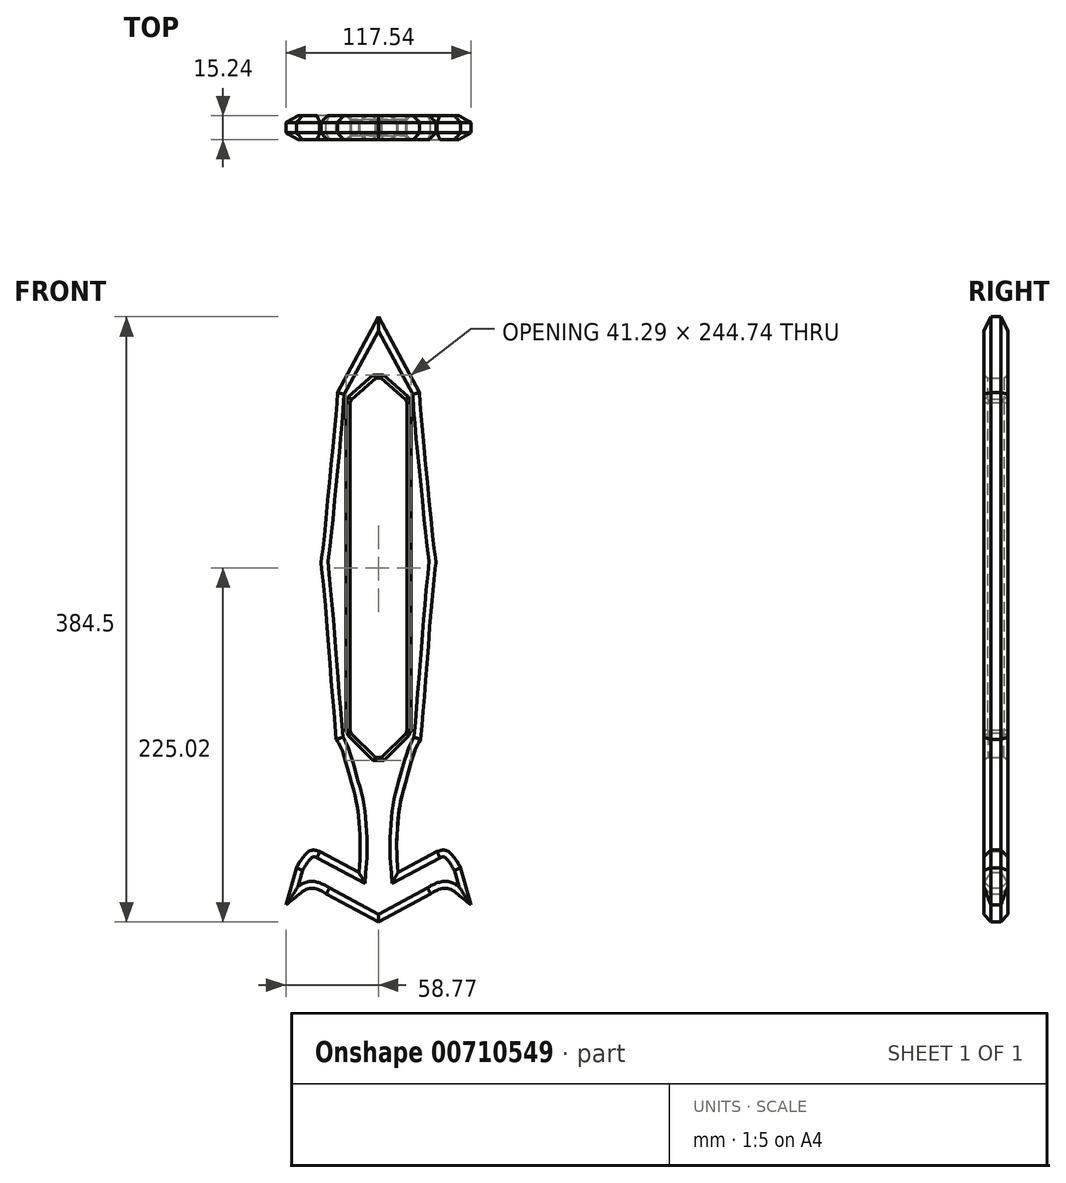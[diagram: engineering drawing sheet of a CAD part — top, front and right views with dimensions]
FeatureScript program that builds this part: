
annotation { "Feature Type Name" : "Feature", "Feature Type Description" : "" }
export const myFeature = defineFeature(function(context is Context, id is Id, definition is map)
    precondition{}
    {
        {
            var Q0;
            Q0=qCreatedBy(makeId("Front.planeOp"),FACE);
            var sketch = newSketch(context, id + "F0", { "sketchPlane" : qUnion([Q0])});
            skFitSpline(sketch, "E0", {"points": [v(-58.77, 10.9) * mm, v(-52.04, 16.33) * mm, v(-46.35, 20.47) * mm, v(-42.08, 21.5) * mm, v(-37.3, 20.2) * mm, v(-33.15, 18) * mm], "startDerivative": vector(27.97, 22.48) * mm, "endDerivative": vector(22.23, -12.93) * mm});
            skLineSegment(sketch, "E1", {"start": v(-33.15, 18) * mm, "end": v(0, 0) * mm});
            skLineSegment(sketch, "E2", {"start": v(0, 0) * mm, "end": v(0, 6.5) * mm});
            skLineSegment(sketch, "E3", {"start": v(-58.77, 10.9) * mm, "end": v(-52.17, 34.44) * mm});
            skFitSpline(sketch, "E4", {"points": [v(-52.17, 34.44) * mm, v(-48.35, 40.7) * mm, v(-44.15, 44.9) * mm, v(-40.76, 45.72) * mm, v(-37.26, 44.79) * mm], "startDerivative": vector(11.84, 21.29) * mm, "endDerivative": vector(16.46, -5.96) * mm});
            skLineSegment(sketch, "E5", {"start": v(-37.26, 44.79) * mm, "end": v(-12.38, 31.59) * mm});
            skFitSpline(sketch, "E6", {"points": [v(-12.38, 31.59) * mm, v(-11.57, 45.95) * mm, v(-12.01, 59.35) * mm, v(-13.24, 72.07) * mm, v(-15.2, 81.42) * mm, v(-20.04, 98.98) * mm, v(-23.62, 110.2) * mm, v(-26.8, 116.07) * mm], "startDerivative": vector(7.18, 93.5) * mm, "endDerivative": vector(-31.36, 51.49) * mm});
            skFitSpline(sketch, "E7", {"points": [v(-26.8, 116.07) * mm, v(-28.43, 135.58) * mm, v(-30.56, 161.2) * mm, v(-33.27, 195.81) * mm, v(-36.38, 226.72) * mm, v(-36.58, 228.72) * mm, v(-36.26, 231.14) * mm, v(-34.94, 240.06) * mm, v(-32.21, 267.55) * mm, v(-29.1, 299.32) * mm, v(-26.8, 324.09) * mm, v(-26.1, 336.42) * mm], "startDerivative": vector(-16.49, 198.18) * mm, "endDerivative": vector(6.55, 149.17) * mm});
            skLineSegment(sketch, "E8", {"start": v(-26.1, 336.42) * mm, "end": v(0, 384.5) * mm});
            skLineSegment(sketch, "E9.MirrorCS", {"start": v(33.15, 18) * mm, "end": v(0, 0) * mm});
            skFitSpline(sketch, "E10.MirrorCS", {"points": [v(58.77, 10.9) * mm, v(52.04, 16.33) * mm, v(46.35, 20.47) * mm, v(42.08, 21.5) * mm, v(37.3, 20.2) * mm, v(33.15, 18) * mm], "startDerivative": vector(-27.97, 22.48) * mm, "endDerivative": vector(-22.23, -12.93) * mm});
            skLineSegment(sketch, "E11.MirrorCS", {"start": v(37.26, 44.79) * mm, "end": v(12.38, 31.59) * mm});
            skLineSegment(sketch, "E12.MirrorCS", {"start": v(58.77, 10.9) * mm, "end": v(52.17, 34.44) * mm});
            skFitSpline(sketch, "E13.MirrorCS", {"points": [v(52.17, 34.44) * mm, v(48.35, 40.7) * mm, v(44.15, 44.9) * mm, v(40.76, 45.72) * mm, v(37.26, 44.79) * mm], "startDerivative": vector(-11.84, 21.29) * mm, "endDerivative": vector(-16.46, -5.96) * mm});
            skFitSpline(sketch, "E14.MirrorCS", {"points": [v(12.38, 31.59) * mm, v(11.57, 45.95) * mm, v(12.01, 59.35) * mm, v(13.24, 72.07) * mm, v(15.2, 81.42) * mm, v(20.04, 98.98) * mm, v(23.62, 110.2) * mm, v(26.8, 116.07) * mm], "startDerivative": vector(-7.18, 93.5) * mm, "endDerivative": vector(31.36, 51.49) * mm});
            skFitSpline(sketch, "E15.MirrorCS", {"points": [v(26.8, 116.07) * mm, v(28.43, 135.58) * mm, v(30.56, 161.2) * mm, v(33.27, 195.81) * mm, v(36.38, 226.72) * mm, v(36.58, 228.72) * mm, v(36.26, 231.14) * mm, v(34.94, 240.06) * mm, v(32.21, 267.55) * mm, v(29.1, 299.32) * mm, v(26.8, 324.09) * mm, v(26.1, 336.42) * mm], "startDerivative": vector(16.49, 198.18) * mm, "endDerivative": vector(-6.55, 149.17) * mm});
            skLineSegment(sketch, "E16.MirrorCS", {"start": v(26.1, 336.42) * mm, "end": v(0, 384.5) * mm});
            skSolve(sketch);
        }
        {
            var Q0;
            Q0=makeQuery(id+"F0.imprint","IMPRINT",FACE,{"disambiguationData":[TD([[makeQuery(id+"F0.imprint","IMPRINT",EDGE,{"derivedFrom":sQuery(id+"F0.wireOp",EDGE,"E0")}),1.0]])]});
            extrude(context, id + "F1", {"entities" : qUnion([Q0]), "endBound" : BoundingType.SYMMETRIC, "depth" : 15.24 * mm, "offsetDistance" : 25.4 * mm});
        }
        {
            var Q0;
            Q0=makeQuery(id+"F1.opExtrude","CAP_FACE",FACE,{"disambiguationData":[OSD([sQuery(id+"F0.wireOp",EDGE,"E0"),sQuery(id+"F0.wireOp",EDGE,"E1"),sQuery(id+"F0.wireOp",EDGE,"E3"),sQuery(id+"F0.wireOp",EDGE,"E4"),sQuery(id+"F0.wireOp",EDGE,"E5"),sQuery(id+"F0.wireOp",EDGE,"E6"),sQuery(id+"F0.wireOp",EDGE,"E7"),sQuery(id+"F0.wireOp",EDGE,"E8"),sQuery(id+"F0.wireOp",EDGE,"E9.MirrorCS"),sQuery(id+"F0.wireOp",EDGE,"E10.MirrorCS"),sQuery(id+"F0.wireOp",EDGE,"E11.MirrorCS"),sQuery(id+"F0.wireOp",EDGE,"E12.MirrorCS"),sQuery(id+"F0.wireOp",EDGE,"E13.MirrorCS"),sQuery(id+"F0.wireOp",EDGE,"E14.MirrorCS"),sQuery(id+"F0.wireOp",EDGE,"E15.MirrorCS"),sQuery(id+"F0.wireOp",EDGE,"E16.MirrorCS")])],"isStart":true});
            var Q1;
            Q1=makeQuery(id+"F1.opExtrude","CAP_FACE",FACE,{"disambiguationData":[OSD([sQuery(id+"F0.wireOp",EDGE,"E0"),sQuery(id+"F0.wireOp",EDGE,"E1"),sQuery(id+"F0.wireOp",EDGE,"E3"),sQuery(id+"F0.wireOp",EDGE,"E4"),sQuery(id+"F0.wireOp",EDGE,"E5"),sQuery(id+"F0.wireOp",EDGE,"E6"),sQuery(id+"F0.wireOp",EDGE,"E7"),sQuery(id+"F0.wireOp",EDGE,"E8"),sQuery(id+"F0.wireOp",EDGE,"E9.MirrorCS"),sQuery(id+"F0.wireOp",EDGE,"E10.MirrorCS"),sQuery(id+"F0.wireOp",EDGE,"E11.MirrorCS"),sQuery(id+"F0.wireOp",EDGE,"E12.MirrorCS"),sQuery(id+"F0.wireOp",EDGE,"E13.MirrorCS"),sQuery(id+"F0.wireOp",EDGE,"E14.MirrorCS"),sQuery(id+"F0.wireOp",EDGE,"E15.MirrorCS"),sQuery(id+"F0.wireOp",EDGE,"E16.MirrorCS")])],"isStart":false});
            chamfer(context, id + "F2", {"entities" : qUnion([Q0, Q1]), "chamferType" : ChamferType.OFFSET_ANGLE, "width" : 4.32 * mm, "oppositeDirection" : false, "angle" : 45 * degree, "tangentPropagation" : true});
        }
        {
            var Q0;
            Q0=qCreatedBy(makeId("Front.planeOp"),FACE);
            var sketch = newSketch(context, id + "F3", { "sketchPlane" : qUnion([Q0])});
            skLineSegment(sketch, "E17", {"start": v(0, 102.67) * mm, "end": v(18.1, 120.66) * mm});
            skLineSegment(sketch, "E18", {"start": v(18.1, 120.66) * mm, "end": v(18.1, 331.1) * mm});
            skLineSegment(sketch, "E19", {"start": v(18.1, 331.1) * mm, "end": v(0, 346.95) * mm});
            skLineSegment(sketch, "E20", {"start": v(0, 346.95) * mm, "end": v(0, 335.17) * mm});
            skLineSegment(sketch, "E21.MirrorCS", {"start": v(-18.1, 331.1) * mm, "end": v(0, 346.95) * mm});
            skLineSegment(sketch, "E22.MirrorCS", {"start": v(-18.1, 120.66) * mm, "end": v(-18.1, 331.1) * mm});
            skLineSegment(sketch, "E23.MirrorCS", {"start": v(0, 102.67) * mm, "end": v(-18.1, 120.66) * mm});
            skSolve(sketch);
        }
        {
            var Q0;
            Q0=makeQuery(id+"F3.imprint","IMPRINT",FACE,{"disambiguationData":[TD([[makeQuery(id+"F3.imprint","IMPRINT",EDGE,{"derivedFrom":sQuery(id+"F3.wireOp",EDGE,"E17")}),1.0]])]});
            extrude(context, id + "F4", {"entities" : qUnion([Q0]), "operationType" : NewBodyOperationType.REMOVE, "oppositeDirection" : true, "depth" : 25.4 * mm, "offsetDistance" : 25.4 * mm});
        }
        {
            var Q0;
            Q0=makeQuery(id+"F4.boolean.opBoolean","COPY",FACE,{"derivedFrom":makeQuery(id+"F4.opExtrude","CAP_FACE",FACE,{"disambiguationData":[OSD([sQuery(id+"F3.wireOp",EDGE,"E17"),sQuery(id+"F3.wireOp",EDGE,"E18"),sQuery(id+"F3.wireOp",EDGE,"E19"),sQuery(id+"F3.wireOp",EDGE,"E21.MirrorCS"),sQuery(id+"F3.wireOp",EDGE,"E22.MirrorCS"),sQuery(id+"F3.wireOp",EDGE,"E23.MirrorCS")])],"isStart":true})});
            extrude(context, id + "F5", {"entities" : qUnion([Q0]), "operationType" : NewBodyOperationType.REMOVE, "oppositeDirection" : true, "depth" : 25.4 * mm, "offsetDistance" : 25.4 * mm});
        }
        {
            var Q0;
            {var subQ0=sQuery(id+"F3.wireOp",EDGE,"E22.MirrorCS");Q0=makeQuery(id+"F5.boolean.opBoolean","MERGE",FACE,{"derivedFrom":[makeQuery(id+"F4.boolean.opBoolean","COPY",FACE,{"derivedFrom":makeQuery(id+"F4.opExtrude","SWEPT_FACE",FACE,{"disambiguationData":[OSD([subQ0])]})})],"fromTools":[makeQuery(id+"F5.opExtrude","SWEPT_FACE",FACE,{"disambiguationData":[OSD([subQ0])]})]});}
            var Q1;
            {var subQ0=sQuery(id+"F3.wireOp",EDGE,"E23.MirrorCS");Q1=makeQuery(id+"F5.boolean.opBoolean","MERGE",FACE,{"derivedFrom":[makeQuery(id+"F4.boolean.opBoolean","COPY",FACE,{"derivedFrom":makeQuery(id+"F4.opExtrude","SWEPT_FACE",FACE,{"disambiguationData":[OSD([subQ0])]})})],"fromTools":[makeQuery(id+"F5.opExtrude","SWEPT_FACE",FACE,{"disambiguationData":[OSD([subQ0])]})]});}
            var Q2;
            {var subQ0=sQuery(id+"F3.wireOp",EDGE,"E21.MirrorCS");Q2=makeQuery(id+"F5.boolean.opBoolean","MERGE",FACE,{"derivedFrom":[makeQuery(id+"F4.boolean.opBoolean","COPY",FACE,{"derivedFrom":makeQuery(id+"F4.opExtrude","SWEPT_FACE",FACE,{"disambiguationData":[OSD([subQ0])]})})],"fromTools":[makeQuery(id+"F5.opExtrude","SWEPT_FACE",FACE,{"disambiguationData":[OSD([subQ0])]})]});}
            var Q3;
            {var subQ0=sQuery(id+"F3.wireOp",EDGE,"E19");Q3=makeQuery(id+"F5.boolean.opBoolean","MERGE",FACE,{"derivedFrom":[makeQuery(id+"F4.boolean.opBoolean","COPY",FACE,{"derivedFrom":makeQuery(id+"F4.opExtrude","SWEPT_FACE",FACE,{"disambiguationData":[OSD([subQ0])]})})],"fromTools":[makeQuery(id+"F5.opExtrude","SWEPT_FACE",FACE,{"disambiguationData":[OSD([subQ0])]})]});}
            var Q4;
            {var subQ0=sQuery(id+"F3.wireOp",EDGE,"E18");Q4=makeQuery(id+"F5.boolean.opBoolean","MERGE",FACE,{"derivedFrom":[makeQuery(id+"F4.boolean.opBoolean","COPY",FACE,{"derivedFrom":makeQuery(id+"F4.opExtrude","SWEPT_FACE",FACE,{"disambiguationData":[OSD([subQ0])]})})],"fromTools":[makeQuery(id+"F5.opExtrude","SWEPT_FACE",FACE,{"disambiguationData":[OSD([subQ0])]})]});}
            var Q5;
            {var subQ0=sQuery(id+"F3.wireOp",EDGE,"E17");Q5=makeQuery(id+"F5.boolean.opBoolean","MERGE",FACE,{"derivedFrom":[makeQuery(id+"F4.boolean.opBoolean","COPY",FACE,{"derivedFrom":makeQuery(id+"F4.opExtrude","SWEPT_FACE",FACE,{"disambiguationData":[OSD([subQ0])]})})],"fromTools":[makeQuery(id+"F5.opExtrude","SWEPT_FACE",FACE,{"disambiguationData":[OSD([subQ0])]})]});}
            chamfer(context, id + "F6", {"entities" : qUnion([Q0, Q1, Q2, Q3, Q4, Q5]), "width" : 2.54 * mm, "tangentPropagation" : true});
        }
    });
